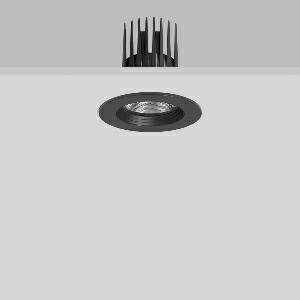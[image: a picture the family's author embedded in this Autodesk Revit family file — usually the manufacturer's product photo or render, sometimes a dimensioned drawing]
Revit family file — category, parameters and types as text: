
# Revit family: heledon_mini_e_901742_003_1_76_7616
name_source: partatom
category: Lighting Fixtures
units: mm (PartAtom-declared; Revit-internal decimal feet)

## family parameters
Cut with Voids When Loaded = No
Host = Face
Light Source = No
Part Type = Normal
Room Calculation Point = No
Round Connector Dimension = Use Diameter
Shared = No

## types (1)
- HELEDON mini E (1 x LED Modul 940, 2750 lm, 4000)
    Apparent Load = 20 VA
    Approval mark = CE
    CIE Flux Codes = 95 99 100 100 100
    Color Rendering = 92
    Color Temperature = 4000
    Default Elevation = 1800 mm
    Description = Series: HELEDON mini
Round recessed downlight. Housing: die-cast aluminium, powder-coated. Black plastic ring and recessed LED to prevent glare from the side. Optical assembly with reflector made of MIRO-Silver with 98% total light reflection for outstanding efficiency - can be changed without tools. Best colour rendering index Ra>90. Suitable for Recessed ceiling mounting. Installation without tools thanks to spring fastening system. Including separate LED converter with connecting cable 600 mm.High quality converter without flickering and stroboscopic effect. Through-wiring box (5 pole) available as accessory. The following accessories can be mounted without use of tools: interchangeable lenses, decorative glasses, honeycomb louvre, clear and frosted diffusers, white interchangeable plastic ring. 
Colour: deep black, matt (RAL 9005)
Diameter: 124 mm
Height: 3 mm
Cut-out diameter: 114 mm
Recess height: 170 mm
Luminaire: recess height: 120 mm
Lamp: LED
Socket: without socket
Colour temperature: 4000K
Colour rendering index (CRI): 92
System power: 20 W
Rated luminous flux: 2750 lm
Luminous efficiency: 138 lm/W
Control gear: Converter, dimmable, DALI
Protection class: II
Type of protection: IP 20
    Height = 0 mm  [stored 0 ft]
    Lamp = 1 x LED Modul 940
    Lamp Light Flux = 2750 lm
    Lamp count = 1
    Length = 124 mm  [stored 0.406824 ft]
    Lifetime = 50000 h
    Luminous efficacy = 138 lm/W
    Manufacturer = RZB
    ModVariant = No
    Model = 901742.003.1.76
    Mounting Place = Ceiling
    Mounting Type = Recessed
    Number of Poles = 1
    OnlyDefault = Yes
    Power Factor = 1
    Product Name = HELEDON mini E
    Product group = Recessed downlights
    ProductGroupID = 402
    Protection Class = Protection class II
    Protection Degree = IP 20
    RLX_Detail_Level = 1
    RLX_Emergency_Light_Flux = 0 lm
    RLX_Emergency_Type = 0
    RLX_Emergency_Type_DB = No
    RlxData = <blob elided: 125753 chars, md5=3c78ed05>
    Socket = socket
    Standby Power = 0 W
    System Light Flux = 2750 lm
    System Power = 20 W
    Type Comments = Product without accessories
    Type Image = 901657.003.jpg
    URL = http://relux.com
    VarID = ---
    Voltage = 230 V
    Voltage Range = 220-240 V
    Weight = 0.00 kg
    Width = 0 mm  [stored 0 ft]

note: [stored X ft] marks values corroborated as IEEE doubles in the binary element streams (Revit-internal decimal feet)

## geometry (parser evidence)
native form markers: Blend x4, Sweep x12
no freeform markers — native parametric forms only
